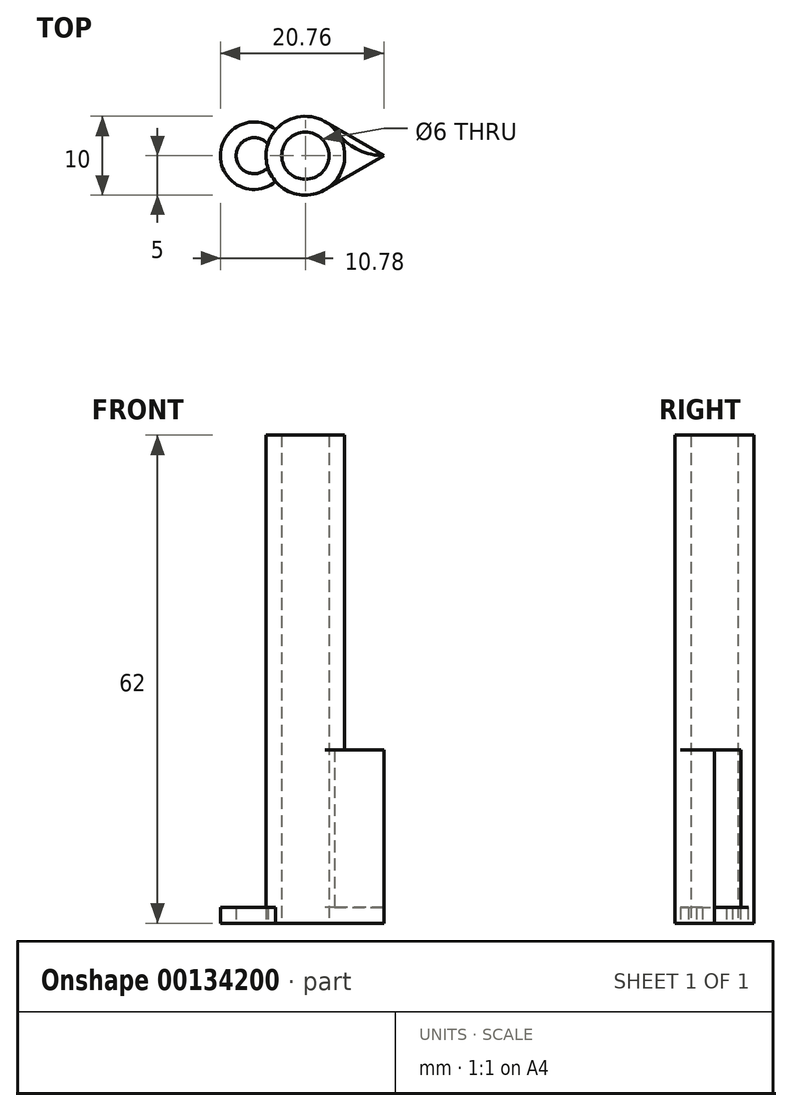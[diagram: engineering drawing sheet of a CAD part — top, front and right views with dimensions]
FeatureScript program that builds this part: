
annotation { "Feature Type Name" : "Feature", "Feature Type Description" : "" }
export const myFeature = defineFeature(function(context is Context, id is Id, definition is map)
    precondition{}
    {
        {
            var Q0;
            Q0=qCreatedBy(makeId("Top.planeOp"),FACE);
            var sketch = newSketch(context, id + "F0", { "sketchPlane" : qUnion([Q0])});
            skCircle(sketch, "E0", {"center": v(0, 0) * mm, "radius": 3 * mm});
            skArc(sketch, "E1.0", {"start": v(4.25, 2.64) * mm, "mid": v(-4.85, 1.21) * mm, "end": v(2.5, -4.33) * mm});
            skLineSegment(sketch, "E2", {"start": v(0, 0) * mm, "end": v(-5, 0) * mm});
            skLineSegment(sketch, "E3", {"start": v(-5, 0) * mm, "end": v(3, 0) * mm});
            skLineSegment(sketch, "E4", {"start": v(9.98, 0) * mm, "end": v(2.5, -4.33) * mm});
            skArc(sketch, "E5", {"start": v(3.7, 3.37) * mm, "mid": v(6.41, 0.9) * mm, "end": v(9.98, 0) * mm});
            skSolve(sketch);
        }
        {
            var Q0;
            {var subQ0=sQuery(id+"F0.wireOp",EDGE,"E4");Q0=makeQuery(id+"F0.imprint","IMPRINT",FACE,{"disambiguationData":[TD([[makeQuery(id+"F0.imprint","IMPRINT",EDGE,{"derivedFrom":subQ0}),-1.0]])]});}
            extrude(context, id + "F1", {"entities" : qUnion([Q0]), "depth" : 20 * mm});
        }
        {
            var Q0;
            Q0=makeQuery(id+"F1.opExtrude","CAP_FACE",FACE,{"disambiguationData":[OSD([sQuery(id+"F0.wireOp",EDGE,"E0"),sQuery(id+"F0.wireOp",EDGE,"E1.0"),sQuery(id+"F0.wireOp",EDGE,"E4"),sQuery(id+"F0.wireOp",EDGE,"E5")])],"isStart":false});
            var sketch = newSketch(context, id + "F2", { "sketchPlane" : qUnion([Q0])});
            skCircle(sketch, "E6", {"center": v(0, 0) * mm, "radius": 5 * mm});
            skCircle(sketch, "E7", {"center": v(0, 0) * mm, "radius": 3 * mm});
            skSolve(sketch);
        }
        {
            var Q0;
            Q0 = qSketchRegion(id + "F2", true);
            extrude(context, id + "F3", {"entities" : qUnion([Q0]), "operationType" : NewBodyOperationType.ADD, "depth" : 40 * mm});
        }
        {
            var Q0;
            Q0=makeQuery(id+"F1.opExtrude","CAP_FACE",FACE,{"disambiguationData":[OSD([sQuery(id+"F0.wireOp",EDGE,"E0"),sQuery(id+"F0.wireOp",EDGE,"E1.0"),sQuery(id+"F0.wireOp",EDGE,"E4"),sQuery(id+"F0.wireOp",EDGE,"E5")])],"isStart":true});
            var sketch = newSketch(context, id + "F4", { "sketchPlane" : qUnion([Q0])});
            skLineSegment(sketch, "E8", {"start": v(9.98, 0) * mm, "end": v(2.5, -4.33) * mm});
            skArc(sketch, "E9.0", {"start": v(3.7, -3.37) * mm, "mid": v(-4.94, -0.76) * mm, "end": v(2.5, 4.33) * mm});
            skLineSegment(sketch, "E10.0", {"start": v(9.98, 0) * mm, "end": v(2.5, 4.33) * mm});
            skCircle(sketch, "E11.0", {"center": v(0, 0) * mm, "radius": 3 * mm});
            skSolve(sketch);
        }
        {
            var Q0;
            {var subQ3=sQuery(id+"F4.wireOp",EDGE,"E10.0");Q0=makeQuery(id+"F4.imprint","IMPRINT",FACE,{"disambiguationData":[TD([[makeQuery(id+"F4.imprint","IMPRINT",EDGE,{"derivedFrom":subQ3}),1.0]])]});}
            var Q1;
            {var subQ0=sQuery(id+"F4.wireOp",EDGE,"E8");Q1=makeQuery(id+"F4.imprint","IMPRINT",FACE,{"disambiguationData":[TD([[makeQuery(id+"F4.imprint","IMPRINT",EDGE,{"derivedFrom":subQ0}),-1.0]])]});}
            extrude(context, id + "F5", {"entities" : qUnion([Q0, Q1]), "operationType" : NewBodyOperationType.ADD, "depth" : 2 * mm});
        }
        {
            var Q0;
            Q0=makeQuery(id+"F5.opExtrude","CAP_FACE",FACE,{"disambiguationData":[OSD([sQuery(id+"F4.wireOp",EDGE,"E8"),sQuery(id+"F4.wireOp",EDGE,"E9.0"),sQuery(id+"F4.wireOp",EDGE,"E10.0"),sQuery(id+"F4.wireOp",EDGE,"E11.0")])],"isStart":false});
            var sketch = newSketch(context, id + "F6", { "sketchPlane" : qUnion([Q0])});
            skLineSegment(sketch, "E12", {"start": v(0, 0) * mm, "end": v(0, -3) * mm});
            skLineSegment(sketch, "E13", {"start": v(0, 0) * mm, "end": v(0, 3) * mm});
            skArc(sketch, "E14", {"start": v(-4.77, 1.5) * mm, "mid": v(-8.78, 0) * mm, "end": v(-4.77, -1.5) * mm});
            skArc(sketch, "E15.0", {"start": v(-3.76, 3.3) * mm, "mid": v(-10.78, 0) * mm, "end": v(-3.76, -3.3) * mm});
            skPoint(sketch, "E16.end.orphan", {"position": v(-4, 0) * mm});
            skArc(sketch, "E17.0", {"start": v(2.5, -4.33) * mm, "mid": v(-5, 0) * mm, "end": v(2.5, 4.33) * mm});
            skPoint(sketch, "E18.start.orphan", {"position": v(0, -1.5) * mm});
            skPoint(sketch, "E19.start.orphan", {"position": v(0, 1.5) * mm});
            skSolve(sketch);
        }
        {
            var Q0;
            {var subQ0=sQuery(id+"F6.wireOp",EDGE,"E14");Q0=makeQuery(id+"F6.imprint","IMPRINT",FACE,{"disambiguationData":[TD([[makeQuery(id+"F6.imprint","IMPRINT",EDGE,{"derivedFrom":subQ0}),-1.0]])]});}
            extrude(context, id + "F7", {"entities" : qUnion([Q0]), "operationType" : NewBodyOperationType.ADD, "oppositeDirection" : true, "depth" : 2 * mm});
        }
    });
